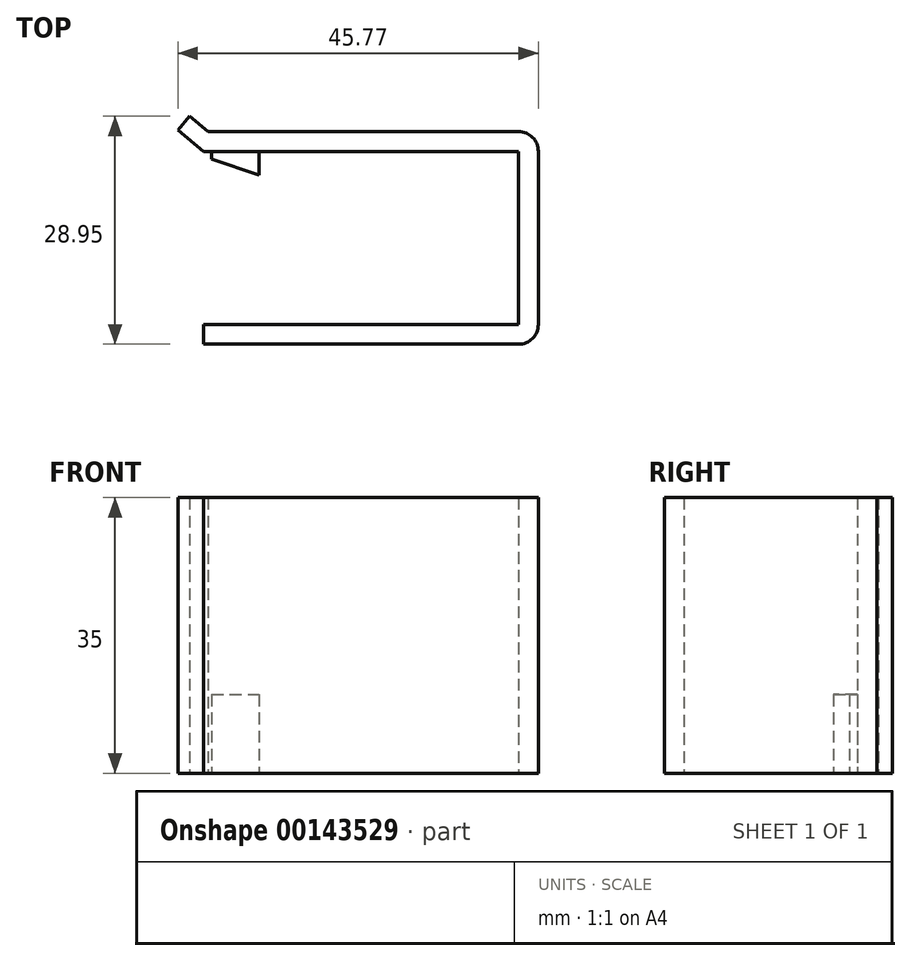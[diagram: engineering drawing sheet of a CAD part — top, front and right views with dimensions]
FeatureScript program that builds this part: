
annotation { "Feature Type Name" : "Feature", "Feature Type Description" : "" }
export const myFeature = defineFeature(function(context is Context, id is Id, definition is map)
    precondition{}
    {
        {
            var Q0;
            Q0=qCreatedBy(makeId("Top.planeOp"),FACE);
            var sketch = newSketch(context, id + "F0", { "sketchPlane" : qUnion([Q0])});
            skLineSegment(sketch, "E0", {"start": v(-20, 11) * mm, "end": v(20, 11) * mm});
            skLineSegment(sketch, "E1", {"start": v(20, 11) * mm, "end": v(20, -11) * mm});
            skLineSegment(sketch, "E2", {"start": v(20, -11) * mm, "end": v(-20, -11) * mm});
            skLineSegment(sketch, "E3", {"start": v(-20, -11) * mm, "end": v(-20, -13.5) * mm});
            skLineSegment(sketch, "E4", {"start": v(-20, -13.5) * mm, "end": v(22.5, -13.5) * mm});
            skLineSegment(sketch, "E5", {"start": v(22.5, -13.5) * mm, "end": v(22.5, 13.5) * mm});
            skLineSegment(sketch, "E6", {"start": v(22.5, 13.5) * mm, "end": v(-20, 13.5) * mm});
            skLineSegment(sketch, "E7", {"start": v(-20, 13.5) * mm, "end": v(-20, 11) * mm});
            skSolve(sketch);
        }
        {
            var Q0;
            Q0 = qSketchRegion(id + "F0", true);
            extrude(context, id + "F1", {"entities" : qUnion([Q0]), "depth" : 35 * mm});
        }
        {
            var Q0;
            Q0=makeQuery(id+"F1.opExtrude","CAP_FACE",FACE,{"disambiguationData":[OSD([sQuery(id+"F0.wireOp",EDGE,"E0"),sQuery(id+"F0.wireOp",EDGE,"E1"),sQuery(id+"F0.wireOp",EDGE,"E2"),sQuery(id+"F0.wireOp",EDGE,"E3"),sQuery(id+"F0.wireOp",EDGE,"E4"),sQuery(id+"F0.wireOp",EDGE,"E5"),sQuery(id+"F0.wireOp",EDGE,"E6"),sQuery(id+"F0.wireOp",EDGE,"E7")])],"isStart":true});
            var sketch = newSketch(context, id + "F2", { "sketchPlane" : qUnion([Q0])});
            skLineSegment(sketch, "E8", {"start": v(-13, -11) * mm, "end": v(-13, -8) * mm});
            skLineSegment(sketch, "E9", {"start": v(-13, -8) * mm, "end": v(-19, -10) * mm});
            skLineSegment(sketch, "E10", {"start": v(-19, -10) * mm, "end": v(-19, -11) * mm});
            skSolve(sketch);
        }
        {
            var Q0;
            Q0 = qSketchRegion(id + "F2", true);
            var Q1;
            {var subQ0=sQuery(id+"F2.wireOp",EDGE,"E8");Q1=makeQuery(id+"F2.imprint","IMPRINT",FACE,{"disambiguationData":[TD([[makeQuery(id+"F2.imprint","IMPRINT",EDGE,{"derivedFrom":subQ0}),1.0]])]});}
            extrude(context, id + "F3", {"entities" : qUnion([Q0, Q1]), "operationType" : NewBodyOperationType.ADD, "oppositeDirection" : true, "depth" : 10 * mm});
        }
        {
            var Q0;
            {var subQ0=sQuery(id+"F0.wireOp",EDGE,"E0");Q0=makeQuery(id+"F3.boolean.opBoolean","MERGE",FACE,{"derivedFrom":[makeQuery(id+"F1.opExtrude","CAP_FACE",FACE,{"disambiguationData":[OSD([subQ0,sQuery(id+"F0.wireOp",EDGE,"E1"),sQuery(id+"F0.wireOp",EDGE,"E2"),sQuery(id+"F0.wireOp",EDGE,"E3"),sQuery(id+"F0.wireOp",EDGE,"E4"),sQuery(id+"F0.wireOp",EDGE,"E5"),sQuery(id+"F0.wireOp",EDGE,"E6"),sQuery(id+"F0.wireOp",EDGE,"E7")])],"isStart":true}),makeQuery(id+"F3.opExtrude","CAP_FACE",FACE,{"disambiguationData":[OSD([subQ0,sQuery(id+"F2.wireOp",EDGE,"E8"),sQuery(id+"F2.wireOp",EDGE,"E9"),sQuery(id+"F2.wireOp",EDGE,"E10")])],"isStart":true})]});}
            var sketch = newSketch(context, id + "F4", { "sketchPlane" : qUnion([Q0])});
            skLineSegment(sketch, "E11", {"start": v(-20, -11) * mm, "end": v(-23.27, -13.7) * mm});
            skLineSegment(sketch, "E12", {"start": v(-23.27, -13.7) * mm, "end": v(-21.82, -15.45) * mm});
            skLineSegment(sketch, "E13", {"start": v(-21.82, -15.45) * mm, "end": v(-19.45, -13.5) * mm});
            skSolve(sketch);
        }
        {
            var Q0;
            Q0=makeQuery(id+"F4.imprint","IMPRINT",FACE,{"disambiguationData":[TD([[makeQuery(id+"F4.imprint","IMPRINT",EDGE,{"derivedFrom":sQuery(id+"F4.wireOp",EDGE,"E11")}),1.0]])]});
            extrude(context, id + "F5", {"entities" : qUnion([Q0]), "operationType" : NewBodyOperationType.ADD, "oppositeDirection" : true, "depth" : 35 * mm});
        }
        {
            var Q0;
            Q0=makeQuery(id+"F1.opExtrude","SWEPT_EDGE",EDGE,{"disambiguationData":[OSD([sQuery(id+"F0.wireOp",EDGE,"E5"),sQuery(id+"F0.wireOp",EDGE,"E6")])]});
            var Q1;
            Q1=makeQuery(id+"F1.opExtrude","SWEPT_EDGE",EDGE,{"disambiguationData":[OSD([sQuery(id+"F0.wireOp",EDGE,"E4"),sQuery(id+"F0.wireOp",EDGE,"E5")])]});
            fillet(context, id + "F6", {"entities" : qUnion([Q0, Q1]), "radius" : 2.5 * mm, "tangentPropagation" : true, "allowEdgeOverflow" : false});
        }
    });
